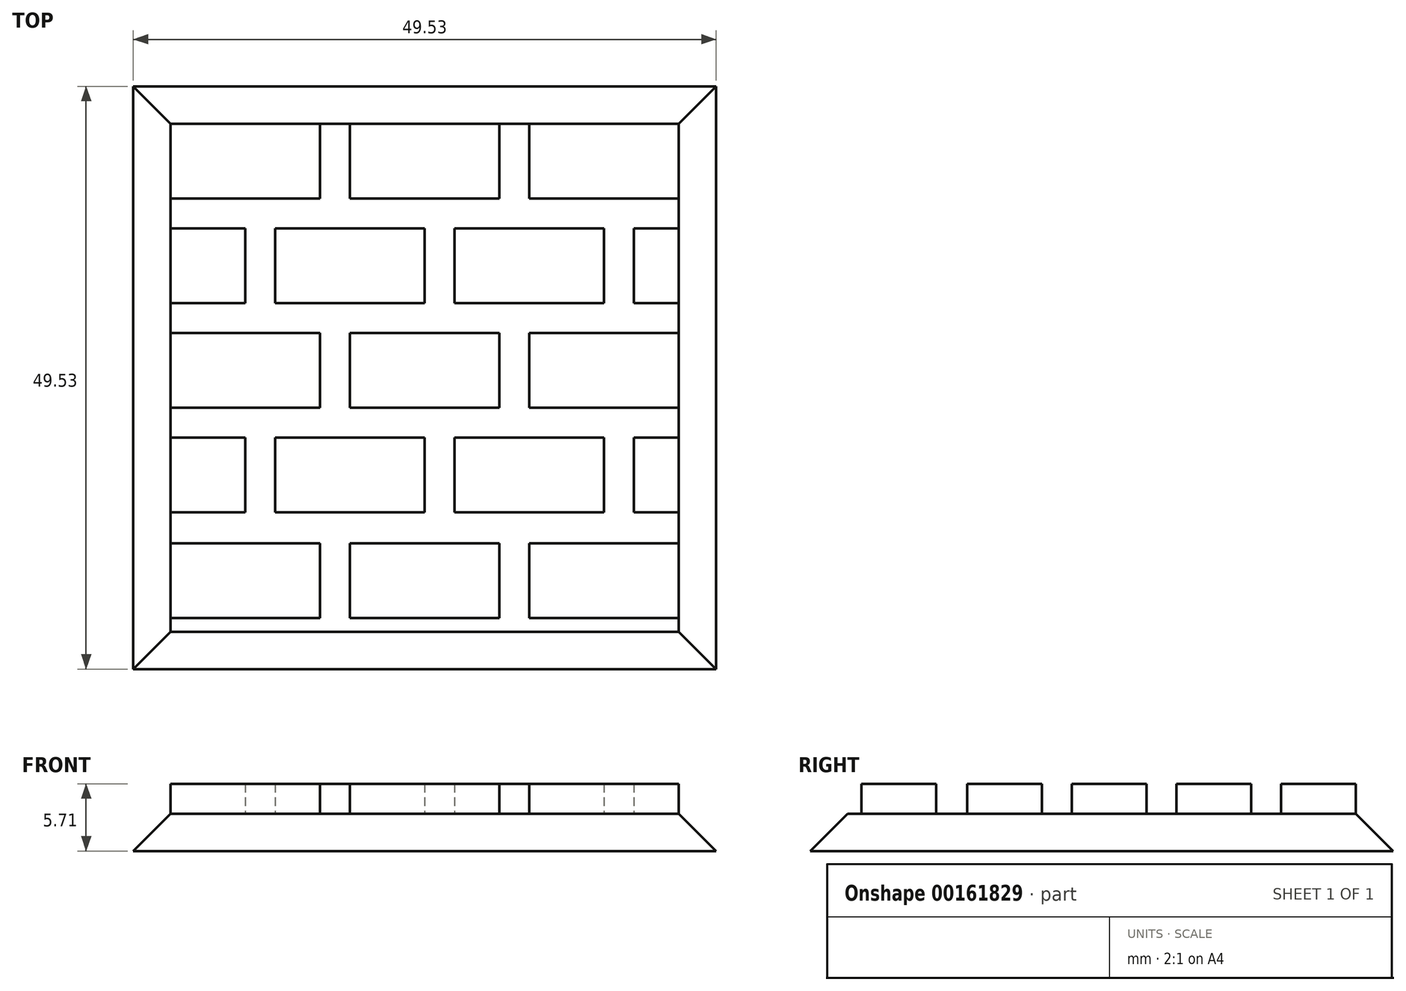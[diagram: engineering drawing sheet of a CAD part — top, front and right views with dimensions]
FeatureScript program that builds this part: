
annotation { "Feature Type Name" : "Feature", "Feature Type Description" : "" }
export const myFeature = defineFeature(function(context is Context, id is Id, definition is map)
    precondition{}
    {
        {
            var Q0;
            Q0=qCreatedBy(makeId("Top.planeOp"),FACE);
            var sketch = newSketch(context, id + "F0", { "sketchPlane" : qUnion([Q0])});
            skLineSegment(sketch, "E0.bottom", {"start": v(0, 0) * mm, "end": v(49.53, 0) * mm});
            skLineSegment(sketch, "E0.top", {"start": v(0, 49.53) * mm, "end": v(49.53, 49.53) * mm});
            skLineSegment(sketch, "E0.left", {"start": v(0, 0) * mm, "end": v(0, 49.53) * mm});
            skLineSegment(sketch, "E0.right", {"start": v(49.53, 0) * mm, "end": v(49.53, 49.53) * mm});
            skSolve(sketch);
        }
        {
            var Q0;
            Q0 = qSketchRegion(id + "F0", true);
            extrude(context, id + "F1", {"entities" : qUnion([Q0]), "depth" : 3.17 * mm});
        }
        {
            var Q0;
            Q0=makeQuery(id+"F1.opExtrude","CAP_FACE",FACE,{"disambiguationData":[OSD([sQuery(id+"F0.wireOp",EDGE,"E0.bottom"),sQuery(id+"F0.wireOp",EDGE,"E0.top"),sQuery(id+"F0.wireOp",EDGE,"E0.left"),sQuery(id+"F0.wireOp",EDGE,"E0.right")])],"isStart":false});
            chamfer(context, id + "F2", {"entities" : qUnion([Q0]), "width" : 3.17 * mm, "tangentPropagation" : true});
        }
        {
            var Q0;
            Q0=makeQuery(id+"F1.opExtrude","CAP_FACE",FACE,{"disambiguationData":[OSD([sQuery(id+"F0.wireOp",EDGE,"E0.bottom"),sQuery(id+"F0.wireOp",EDGE,"E0.top"),sQuery(id+"F0.wireOp",EDGE,"E0.left"),sQuery(id+"F0.wireOp",EDGE,"E0.right")])],"isStart":false});
            var sketch = newSketch(context, id + "F3", { "sketchPlane" : qUnion([Q0])});
            skLineSegment(sketch, "E1.bottom", {"start": v(3.18, 46.36) * mm, "end": v(15.88, 46.36) * mm});
            skLineSegment(sketch, "E1.top", {"start": v(3.18, 40) * mm, "end": v(15.88, 40) * mm});
            skLineSegment(sketch, "E1.left", {"start": v(3.18, 46.36) * mm, "end": v(3.18, 40) * mm});
            skLineSegment(sketch, "E1.right", {"start": v(15.88, 46.36) * mm, "end": v(15.88, 40) * mm});
            skLineSegment(sketch, "E2", {"start": v(18.41, 46.36) * mm, "end": v(18.41, 40) * mm});
            skLineSegment(sketch, "E3.bottom", {"start": v(18.41, 40) * mm, "end": v(31.12, 40) * mm});
            skLineSegment(sketch, "E3.top", {"start": v(18.41, 46.36) * mm, "end": v(31.12, 46.36) * mm});
            skLineSegment(sketch, "E3.left", {"start": v(18.41, 40) * mm, "end": v(18.41, 46.36) * mm});
            skLineSegment(sketch, "E3.right", {"start": v(31.12, 40) * mm, "end": v(31.12, 46.36) * mm});
            skLineSegment(sketch, "E4.bottom", {"start": v(33.66, 40) * mm, "end": v(46.35, 40) * mm});
            skLineSegment(sketch, "E4.top", {"start": v(33.66, 46.36) * mm, "end": v(46.35, 46.36) * mm});
            skLineSegment(sketch, "E4.left", {"start": v(33.66, 40) * mm, "end": v(33.66, 46.36) * mm});
            skLineSegment(sketch, "E4.right", {"start": v(46.35, 40) * mm, "end": v(46.35, 46.36) * mm});
            skLineSegment(sketch, "E5.bottom", {"start": v(3.18, 37.47) * mm, "end": v(9.53, 37.47) * mm});
            skLineSegment(sketch, "E5.top", {"start": v(3.18, 31.12) * mm, "end": v(9.53, 31.12) * mm});
            skLineSegment(sketch, "E5.left", {"start": v(3.18, 37.47) * mm, "end": v(3.18, 31.12) * mm});
            skLineSegment(sketch, "E5.right", {"start": v(9.53, 37.47) * mm, "end": v(9.53, 31.12) * mm});
            skLineSegment(sketch, "E6.bottom", {"start": v(12.07, 31.12) * mm, "end": v(24.77, 31.12) * mm});
            skLineSegment(sketch, "E6.top", {"start": v(12.07, 37.47) * mm, "end": v(24.77, 37.47) * mm});
            skLineSegment(sketch, "E6.left", {"start": v(12.07, 31.12) * mm, "end": v(12.07, 37.47) * mm});
            skLineSegment(sketch, "E6.right", {"start": v(24.77, 31.12) * mm, "end": v(24.77, 37.47) * mm});
            skLineSegment(sketch, "E7.bottom", {"start": v(27.3, 31.12) * mm, "end": v(40, 31.12) * mm});
            skLineSegment(sketch, "E7.top", {"start": v(27.3, 37.47) * mm, "end": v(40, 37.47) * mm});
            skLineSegment(sketch, "E7.left", {"start": v(27.3, 31.12) * mm, "end": v(27.3, 37.47) * mm});
            skLineSegment(sketch, "E7.right", {"start": v(40, 31.12) * mm, "end": v(40, 37.47) * mm});
            skLineSegment(sketch, "E8.bottom", {"start": v(42.55, 31.12) * mm, "end": v(46.35, 31.12) * mm});
            skLineSegment(sketch, "E8.top", {"start": v(42.55, 37.47) * mm, "end": v(46.35, 37.47) * mm});
            skLineSegment(sketch, "E8.left", {"start": v(42.55, 31.12) * mm, "end": v(42.55, 37.47) * mm});
            skLineSegment(sketch, "E8.right", {"start": v(46.35, 31.12) * mm, "end": v(46.35, 37.47) * mm});
            skLineSegment(sketch, "E9.bottom", {"start": v(3.18, 3.17) * mm, "end": v(46.35, 3.17) * mm});
            skLineSegment(sketch, "E9.left", {"start": v(3.18, 3.17) * mm, "end": v(3.18, 46.36) * mm});
            skLineSegment(sketch, "E9.right", {"start": v(46.35, 3.17) * mm, "end": v(46.35, 46.36) * mm});
            skLineSegment(sketch, "E10.bottom", {"start": v(3.17, 28.58) * mm, "end": v(15.87, 28.58) * mm});
            skLineSegment(sketch, "E10.top", {"start": v(3.17, 22.23) * mm, "end": v(15.87, 22.23) * mm});
            skLineSegment(sketch, "E10.left", {"start": v(3.17, 28.58) * mm, "end": v(3.17, 22.23) * mm});
            skLineSegment(sketch, "E10.right", {"start": v(15.87, 28.58) * mm, "end": v(15.87, 22.23) * mm});
            skLineSegment(sketch, "E11", {"start": v(18.41, 28.58) * mm, "end": v(18.41, 22.23) * mm});
            skLineSegment(sketch, "E12.bottom", {"start": v(18.41, 22.23) * mm, "end": v(31.11, 22.23) * mm});
            skLineSegment(sketch, "E12.top", {"start": v(18.41, 28.58) * mm, "end": v(31.11, 28.58) * mm});
            skLineSegment(sketch, "E12.left", {"start": v(18.41, 22.23) * mm, "end": v(18.41, 28.58) * mm});
            skLineSegment(sketch, "E12.right", {"start": v(31.11, 22.23) * mm, "end": v(31.11, 28.58) * mm});
            skLineSegment(sketch, "E13.bottom", {"start": v(33.65, 22.23) * mm, "end": v(46.35, 22.23) * mm});
            skLineSegment(sketch, "E13.top", {"start": v(33.65, 28.58) * mm, "end": v(46.35, 28.58) * mm});
            skLineSegment(sketch, "E13.left", {"start": v(33.65, 22.23) * mm, "end": v(33.65, 28.58) * mm});
            skLineSegment(sketch, "E13.right", {"start": v(46.35, 22.23) * mm, "end": v(46.35, 28.58) * mm});
            skLineSegment(sketch, "E14.bottom", {"start": v(3.17, 19.69) * mm, "end": v(9.52, 19.69) * mm});
            skLineSegment(sketch, "E14.top", {"start": v(3.17, 13.34) * mm, "end": v(9.52, 13.34) * mm});
            skLineSegment(sketch, "E14.left", {"start": v(3.17, 19.69) * mm, "end": v(3.17, 13.34) * mm});
            skLineSegment(sketch, "E14.right", {"start": v(9.52, 19.69) * mm, "end": v(9.52, 13.34) * mm});
            skLineSegment(sketch, "E15.bottom", {"start": v(12.06, 13.34) * mm, "end": v(24.76, 13.34) * mm});
            skLineSegment(sketch, "E15.top", {"start": v(12.06, 19.69) * mm, "end": v(24.76, 19.69) * mm});
            skLineSegment(sketch, "E15.left", {"start": v(12.06, 13.34) * mm, "end": v(12.06, 19.69) * mm});
            skLineSegment(sketch, "E15.right", {"start": v(24.76, 13.34) * mm, "end": v(24.76, 19.69) * mm});
            skLineSegment(sketch, "E16.bottom", {"start": v(27.3, 13.34) * mm, "end": v(40, 13.34) * mm});
            skLineSegment(sketch, "E16.top", {"start": v(27.3, 19.69) * mm, "end": v(40, 19.69) * mm});
            skLineSegment(sketch, "E16.left", {"start": v(27.3, 13.34) * mm, "end": v(27.3, 19.69) * mm});
            skLineSegment(sketch, "E16.right", {"start": v(40, 13.34) * mm, "end": v(40, 19.69) * mm});
            skLineSegment(sketch, "E17.bottom", {"start": v(42.54, 13.34) * mm, "end": v(46.35, 13.34) * mm});
            skLineSegment(sketch, "E17.top", {"start": v(42.54, 19.69) * mm, "end": v(46.35, 19.69) * mm});
            skLineSegment(sketch, "E17.left", {"start": v(42.54, 13.34) * mm, "end": v(42.54, 19.69) * mm});
            skLineSegment(sketch, "E17.right", {"start": v(46.35, 13.34) * mm, "end": v(46.35, 19.69) * mm});
            skLineSegment(sketch, "E18.bottom", {"start": v(3.18, 10.7) * mm, "end": v(15.88, 10.7) * mm});
            skLineSegment(sketch, "E18.top", {"start": v(3.18, 4.35) * mm, "end": v(15.88, 4.35) * mm});
            skLineSegment(sketch, "E18.left", {"start": v(3.18, 10.7) * mm, "end": v(3.18, 4.35) * mm});
            skLineSegment(sketch, "E18.right", {"start": v(15.88, 10.7) * mm, "end": v(15.88, 4.35) * mm});
            skLineSegment(sketch, "E19", {"start": v(18.42, 10.7) * mm, "end": v(18.42, 4.35) * mm});
            skLineSegment(sketch, "E20.bottom", {"start": v(18.42, 4.35) * mm, "end": v(31.12, 4.35) * mm});
            skLineSegment(sketch, "E20.top", {"start": v(18.41, 10.7) * mm, "end": v(31.12, 10.7) * mm});
            skLineSegment(sketch, "E20.left", {"start": v(18.42, 4.35) * mm, "end": v(18.42, 10.7) * mm});
            skLineSegment(sketch, "E20.right", {"start": v(31.12, 4.35) * mm, "end": v(31.12, 10.7) * mm});
            skLineSegment(sketch, "E21.bottom", {"start": v(33.65, 4.35) * mm, "end": v(46.35, 4.35) * mm});
            skLineSegment(sketch, "E21.top", {"start": v(33.65, 10.7) * mm, "end": v(46.35, 10.7) * mm});
            skLineSegment(sketch, "E21.left", {"start": v(33.65, 4.35) * mm, "end": v(33.65, 10.7) * mm});
            skLineSegment(sketch, "E21.right", {"start": v(46.35, 4.35) * mm, "end": v(46.35, 10.7) * mm});
            skSolve(sketch);
        }
        {
            var Q0;
            {var subQ0=sQuery(id+"F3.wireOp",EDGE,"E13.bottom");var subQ3=sQuery(id+"F3.wireOp",EDGE,"E17.bottom");var subQ5=sQuery(id+"F3.wireOp",EDGE,"E21.bottom");var subQ7=sQuery(id+"F3.wireOp",EDGE,"E18.bottom");var subQ10=sQuery(id+"F3.wireOp",EDGE,"E14.bottom");var subQ12=sQuery(id+"F3.wireOp",EDGE,"E10.bottom");Q0=qUnion([makeQuery(id+"F3.imprint","IMPRINT",FACE,{"disambiguationData":[TD([[makeQuery(id+"F3.imprint","IMPRINT",EDGE,{"derivedFrom":sQuery(id+"F3.wireOp",EDGE,"E8.bottom")}),1.0]])]}),makeQuery(id+"F3.imprint","IMPRINT",FACE,{"disambiguationData":[TD([[makeQuery(id+"F3.imprint","IMPRINT",EDGE,{"derivedFrom":sQuery(id+"F3.wireOp",EDGE,"E1.bottom")}),1.0]])]}),makeQuery(id+"F3.imprint","IMPRINT",FACE,{"disambiguationData":[TD([[makeQuery(id+"F3.imprint","IMPRINT",EDGE,{"derivedFrom":subQ12}),-1.0]])]}),makeQuery(id+"F3.imprint","IMPRINT",FACE,{"disambiguationData":[TD([[makeQuery(id+"F3.imprint","IMPRINT",EDGE,{"derivedFrom":sQuery(id+"F3.wireOp",EDGE,"E2")}),1.0]])]}),makeQuery(id+"F3.imprint","IMPRINT",FACE,{"disambiguationData":[TD([[makeQuery(id+"F3.imprint","IMPRINT",EDGE,{"derivedFrom":subQ10}),-1.0]])]}),makeQuery(id+"F3.imprint","IMPRINT",FACE,{"disambiguationData":[TD([[makeQuery(id+"F3.imprint","IMPRINT",EDGE,{"derivedFrom":sQuery(id+"F3.wireOp",EDGE,"E4.bottom")}),1.0]])]}),makeQuery(id+"F3.imprint","IMPRINT",FACE,{"disambiguationData":[TD([[makeQuery(id+"F3.imprint","IMPRINT",EDGE,{"derivedFrom":sQuery(id+"F3.wireOp",EDGE,"E16.bottom")}),1.0]])]}),makeQuery(id+"F3.imprint","IMPRINT",FACE,{"disambiguationData":[TD([[makeQuery(id+"F3.imprint","IMPRINT",EDGE,{"derivedFrom":subQ7}),-1.0]])]}),makeQuery(id+"F3.imprint","IMPRINT",FACE,{"disambiguationData":[TD([[makeQuery(id+"F3.imprint","IMPRINT",EDGE,{"derivedFrom":sQuery(id+"F3.wireOp",EDGE,"E5.bottom")}),-1.0]])]}),makeQuery(id+"F3.imprint","IMPRINT",FACE,{"disambiguationData":[TD([[makeQuery(id+"F3.imprint","IMPRINT",EDGE,{"derivedFrom":sQuery(id+"F3.wireOp",EDGE,"E11")}),1.0]])]}),makeQuery(id+"F3.imprint","IMPRINT",FACE,{"disambiguationData":[TD([[makeQuery(id+"F3.imprint","IMPRINT",EDGE,{"derivedFrom":subQ5}),1.0]])]}),makeQuery(id+"F3.imprint","IMPRINT",FACE,{"disambiguationData":[TD([[makeQuery(id+"F3.imprint","IMPRINT",EDGE,{"derivedFrom":sQuery(id+"F3.wireOp",EDGE,"E6.bottom")}),1.0]])]}),makeQuery(id+"F3.imprint","IMPRINT",FACE,{"disambiguationData":[TD([[makeQuery(id+"F3.imprint","IMPRINT",EDGE,{"derivedFrom":sQuery(id+"F3.wireOp",EDGE,"E15.bottom")}),1.0]])]}),makeQuery(id+"F3.imprint","IMPRINT",FACE,{"disambiguationData":[TD([[makeQuery(id+"F3.imprint","IMPRINT",EDGE,{"derivedFrom":subQ3}),1.0]])]}),makeQuery(id+"F3.imprint","IMPRINT",FACE,{"disambiguationData":[TD([[makeQuery(id+"F3.imprint","IMPRINT",EDGE,{"derivedFrom":sQuery(id+"F3.wireOp",EDGE,"E7.bottom")}),1.0]])]}),makeQuery(id+"F3.imprint","IMPRINT",FACE,{"disambiguationData":[TD([[makeQuery(id+"F3.imprint","IMPRINT",EDGE,{"derivedFrom":subQ0}),1.0]])]}),makeQuery(id+"F3.imprint","IMPRINT",FACE,{"disambiguationData":[TD([[makeQuery(id+"F3.imprint","IMPRINT",EDGE,{"derivedFrom":sQuery(id+"F3.wireOp",EDGE,"E19")}),1.0]])]})]);}
            extrude(context, id + "F4", {"entities" : qUnion([Q0]), "operationType" : NewBodyOperationType.ADD, "depth" : 2.54 * mm});
        }
    });
